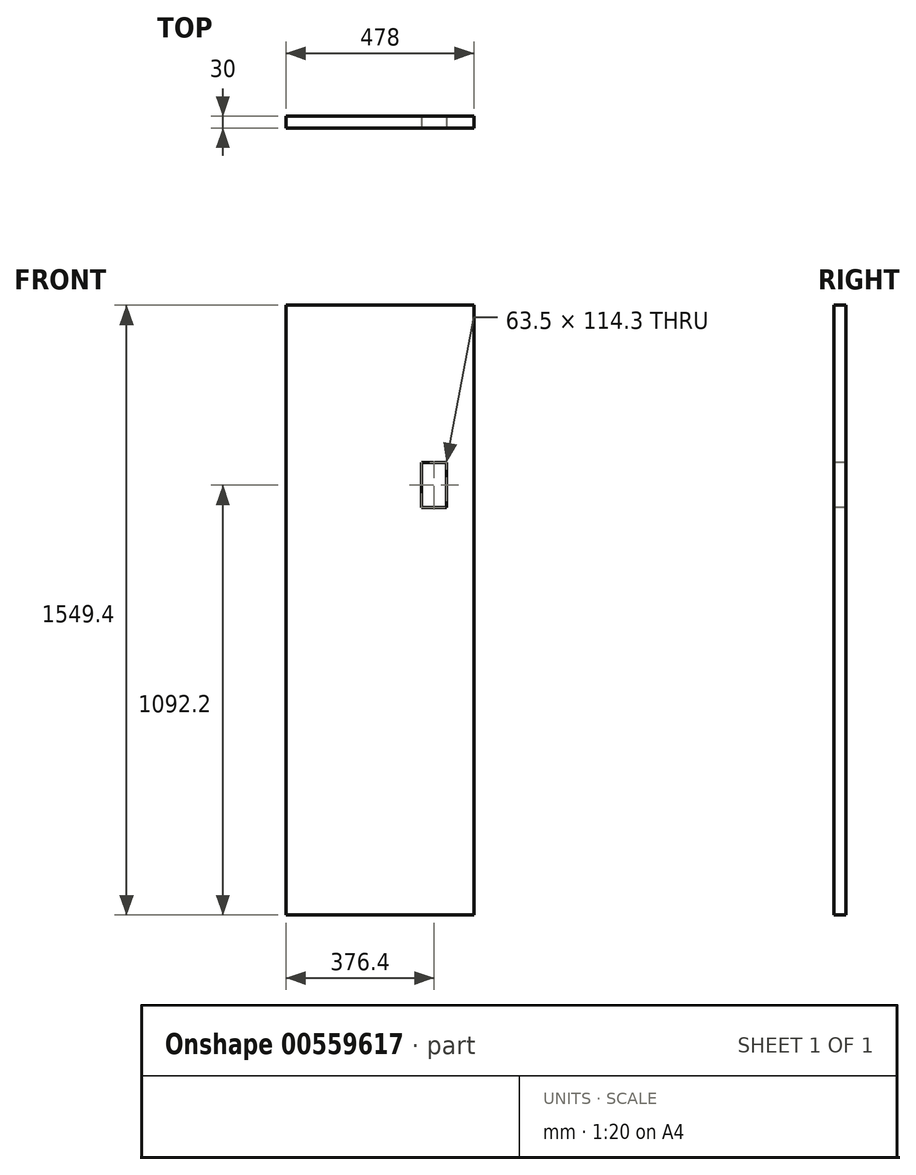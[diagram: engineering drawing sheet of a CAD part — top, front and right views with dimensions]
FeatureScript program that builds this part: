
annotation { "Feature Type Name" : "Feature", "Feature Type Description" : "" }
export const myFeature = defineFeature(function(context is Context, id is Id, definition is map)
    precondition{}
    {
        {
            var Q0;
            Q0=qCreatedBy(makeId("Front.planeOp"),FACE);
            var sketch = newSketch(context, id + "F0", { "sketchPlane" : qUnion([Q0])});
            skLineSegment(sketch, "E0.bottom", {"start": v(-239, -774.7) * mm, "end": v(239, -774.7) * mm});
            skLineSegment(sketch, "E0.top", {"start": v(-239, 774.7) * mm, "end": v(239, 774.7) * mm});
            skLineSegment(sketch, "E0.left", {"start": v(-239, -774.7) * mm, "end": v(-239, 774.7) * mm});
            skLineSegment(sketch, "E0.right", {"start": v(239, -774.7) * mm, "end": v(239, 774.7) * mm});
            skPoint(sketch, "E0.middle", {"position": v(0, 0) * mm});
            skSolve(sketch);
        }
        {
            var Q0;
            Q0 = qSketchRegion(id + "F0", true);
            extrude(context, id + "F1", {"entities" : qUnion([Q0]), "depth" : 30 * mm, "offsetDistance" : 25.4 * mm});
        }
        {
            var Q0;
            Q0=makeQuery(id+"F1.opExtrude","CAP_FACE",FACE,{"disambiguationData":[OSD([sQuery(id+"F0.wireOp",EDGE,"E0.bottom"),sQuery(id+"F0.wireOp",EDGE,"E0.top"),sQuery(id+"F0.wireOp",EDGE,"E0.left"),sQuery(id+"F0.wireOp",EDGE,"E0.right")])],"isStart":false});
            var sketch = newSketch(context, id + "F2", { "sketchPlane" : qUnion([Q0])});
            skLineSegment(sketch, "E1.bottom", {"start": v(105.65, 260.35) * mm, "end": v(169.15, 260.35) * mm});
            skLineSegment(sketch, "E1.top", {"start": v(105.65, 374.65) * mm, "end": v(169.15, 374.65) * mm});
            skLineSegment(sketch, "E1.left", {"start": v(105.65, 260.35) * mm, "end": v(105.65, 374.65) * mm});
            skLineSegment(sketch, "E1.right", {"start": v(169.15, 260.35) * mm, "end": v(169.15, 374.65) * mm});
            skPoint(sketch, "E1.middle", {"position": v(137.4, 317.5) * mm});
            skSolve(sketch);
        }
        {
            var Q0;
            Q0 = qSketchRegion(id + "F2", true);
            extrude(context, id + "F3", {"entities" : qUnion([Q0]), "operationType" : NewBodyOperationType.REMOVE, "endBound" : BoundingType.UP_TO_NEXT, "oppositeDirection" : true, "depth" : 25.4 * mm, "offsetDistance" : 25.4 * mm});
        }
    });
